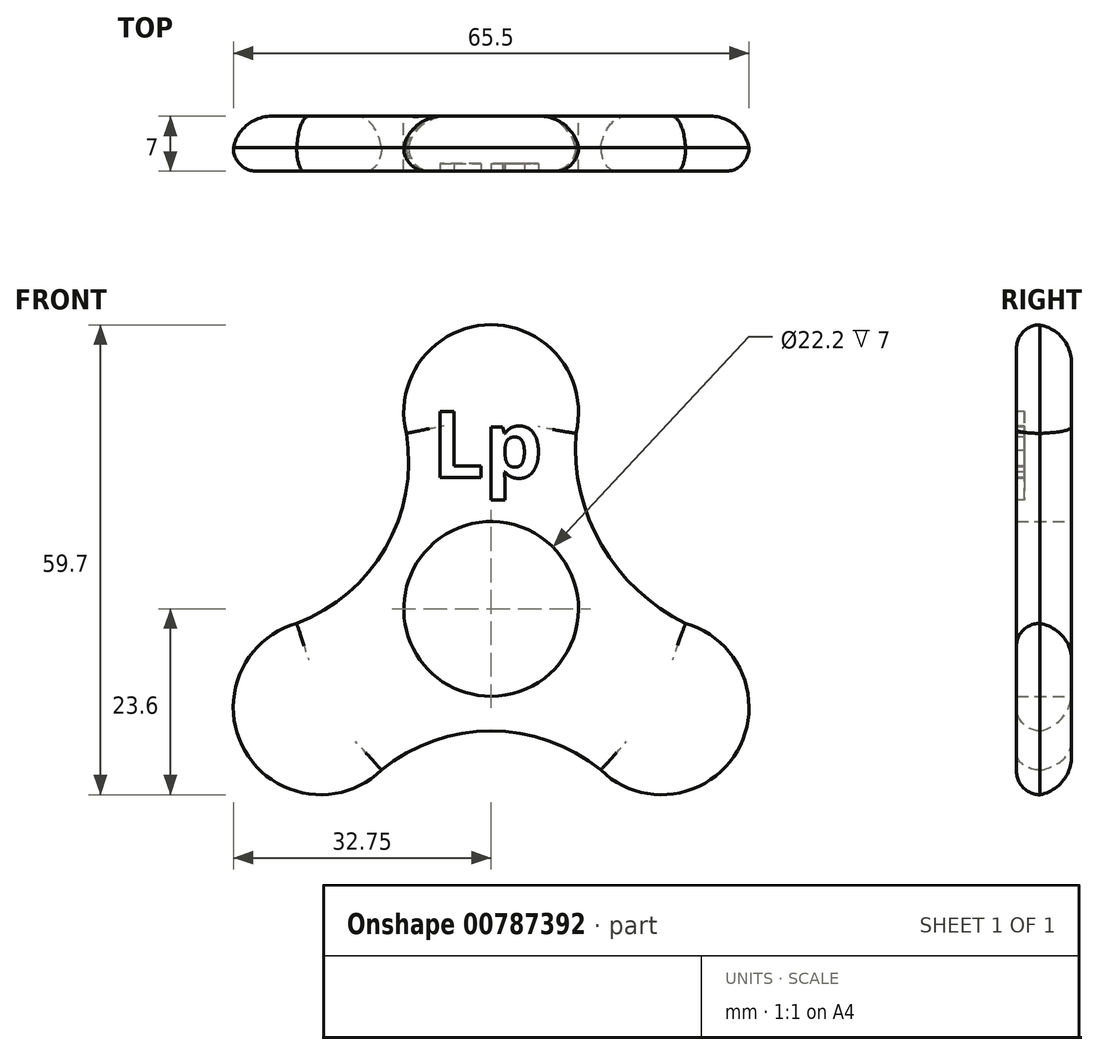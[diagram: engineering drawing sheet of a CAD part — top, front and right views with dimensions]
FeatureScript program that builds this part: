
annotation { "Feature Type Name" : "Feature", "Feature Type Description" : "" }
export const myFeature = defineFeature(function(context is Context, id is Id, definition is map)
    precondition{}
    {
        {
            var Q0;
            Q0=qCreatedBy(makeId("Front.planeOp"),FACE);
            var sketch = newSketch(context, id + "F0", { "sketchPlane" : qUnion([Q0])});
            skCircle(sketch, "E0", {"center": v(0, 0) * mm, "radius": 11.1 * mm});
            skArc(sketch, "E1", {"start": v(10.77, 22.3) * mm, "mid": v(0, 36.1) * mm, "end": v(-10.77, 22.3) * mm});
            skArc(sketch, "E2.1.0", {"start": v(-24.7, -1.83) * mm, "mid": v(-31.26, -18.05) * mm, "end": v(-13.93, -20.48) * mm});
            skArc(sketch, "E2.2.0", {"start": v(13.93, -20.48) * mm, "mid": v(31.26, -18.05) * mm, "end": v(24.7, -1.83) * mm});
            skArc(sketch, "E3", {"start": v(-24.7, -1.83) * mm, "mid": v(-13.43, 7.75) * mm, "end": v(-10.77, 22.3) * mm});
            skArc(sketch, "E4", {"start": v(10.77, 22.3) * mm, "mid": v(14.03, 8.1) * mm, "end": v(24.7, -1.83) * mm});
            skArc(sketch, "E5", {"start": v(13.93, -20.48) * mm, "mid": v(0, -15.5) * mm, "end": v(-13.93, -20.48) * mm});
            skSolve(sketch);
        }
        {
            var Q0;
            Q0 = qSketchRegion(id + "F0", true);
            extrude(context, id + "F1", {"entities" : qUnion([Q0]), "depth" : 7 * mm, "offsetDistance" : 25 * mm});
        }
        {
            var Q0;
            Q0=makeQuery(id+"F1.opExtrude","CAP_EDGE",EDGE,{"disambiguationData":[OSD([sQuery(id+"F0.wireOp",EDGE,"E1")])],"isStart":false});
            var Q1;
            Q1=makeQuery(id+"F1.opExtrude","CAP_EDGE",EDGE,{"disambiguationData":[OSD([sQuery(id+"F0.wireOp",EDGE,"E3")])],"isStart":false});
            var Q2;
            Q2=makeQuery(id+"F1.opExtrude","CAP_EDGE",EDGE,{"disambiguationData":[OSD([sQuery(id+"F0.wireOp",EDGE,"E2.1.0")])],"isStart":false});
            var Q3;
            Q3=makeQuery(id+"F1.opExtrude","CAP_EDGE",EDGE,{"disambiguationData":[OSD([sQuery(id+"F0.wireOp",EDGE,"E5")])],"isStart":false});
            var Q4;
            Q4=makeQuery(id+"F1.opExtrude","CAP_EDGE",EDGE,{"disambiguationData":[OSD([sQuery(id+"F0.wireOp",EDGE,"E2.2.0")])],"isStart":false});
            var Q5;
            Q5=makeQuery(id+"F1.opExtrude","CAP_EDGE",EDGE,{"disambiguationData":[OSD([sQuery(id+"F0.wireOp",EDGE,"E4")])],"isStart":false});
            fillet(context, id + "F2", {"entities" : qUnion([Q0, Q1, Q2, Q3, Q4, Q5]), "radius" : 3 * mm, "tangentPropagation" : true, "allowEdgeOverflow" : false});
        }
        {
            var Q0;
            Q0=makeQuery(id+"F1.opExtrude","CAP_EDGE",EDGE,{"disambiguationData":[OSD([sQuery(id+"F0.wireOp",EDGE,"E2.2.0")])],"isStart":true});
            var Q1;
            Q1=makeQuery(id+"F1.opExtrude","CAP_EDGE",EDGE,{"disambiguationData":[OSD([sQuery(id+"F0.wireOp",EDGE,"E4")])],"isStart":true});
            var Q2;
            Q2=makeQuery(id+"F1.opExtrude","CAP_EDGE",EDGE,{"disambiguationData":[OSD([sQuery(id+"F0.wireOp",EDGE,"E1")])],"isStart":true});
            var Q3;
            Q3=makeQuery(id+"F1.opExtrude","CAP_EDGE",EDGE,{"disambiguationData":[OSD([sQuery(id+"F0.wireOp",EDGE,"E2.1.0")])],"isStart":true});
            fillet(context, id + "F3", {"entities" : qUnion([Q0, Q1, Q2, Q3]), "radius" : 5 * mm, "tangentPropagation" : true, "allowEdgeOverflow" : false});
        }
        {
            var Q0;
            Q0=makeQuery(id+"F1.opExtrude","CAP_FACE",FACE,{"disambiguationData":[OSD([sQuery(id+"F0.wireOp",EDGE,"E0"),sQuery(id+"F0.wireOp",EDGE,"E1"),sQuery(id+"F0.wireOp",EDGE,"E2.1.0"),sQuery(id+"F0.wireOp",EDGE,"E2.2.0"),sQuery(id+"F0.wireOp",EDGE,"E3"),sQuery(id+"F0.wireOp",EDGE,"E4"),sQuery(id+"F0.wireOp",EDGE,"E5")])],"isStart":false});
            var sketch = newSketch(context, id + "F4", { "sketchPlane" : qUnion([Q0])});
            skText(sketch, "E6", { "text": "Lp", "fontName": "OpenSans-Bold.ttf"});
            const initialGuessF4  = {"E6": [-0.00756, 0.0167, 1, 0, 0.00847]};
            skSetInitialGuess(sketch, initialGuessF4);
            skSolve(sketch);
        }
        {
            var Q0;
            Q0 = qSketchRegion(id + "F4", true);
            extrude(context, id + "F5", {"entities" : qUnion([Q0]), "operationType" : NewBodyOperationType.REMOVE, "oppositeDirection" : true, "depth" : 1 * mm, "offsetDistance" : 25 * mm});
        }
    });
